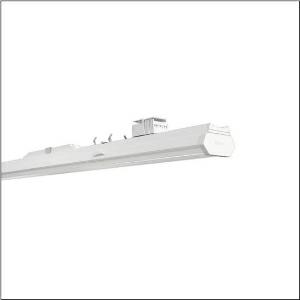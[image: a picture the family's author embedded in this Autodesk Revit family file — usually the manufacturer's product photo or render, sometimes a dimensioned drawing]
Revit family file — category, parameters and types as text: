
# Revit family: licross_21_protected_mo_52tp12dn4a5g3s4
name_source: partatom
category: Lighting Fixtures
units: mm (PartAtom-declared; Revit-internal decimal feet)

## family parameters
Cut with Voids When Loaded = No
Host = Face
Light Source = No
Part Type = Normal
Room Calculation Point = No
Round Connector Dimension = Use Diameter
Shared = No

## types (1)
- --- (1 x LED, 940 lm, 6.8 W, 4000K)
    Apparent Load = 7 VA
    CIE Flux Codes = 73 92 98 99 100
    Color Rendering = 80
    Color Temperature = 4000K
    Default Elevation = 1800 mm
    Description = Licross 21 Protected MO, luminaire insert, of sheet steel, galvanised, coil coated, white, length: 1.500mm, width: 90mm, height: 103mm, LED rated luminous flux: 10.700lm, light colour: 840, SDCM (Standard Deviation of Colour Matching)MacAdam ≤ 3 SDCM (initial), control gear: DALI 2, with plug, 6-pole, with phase selection, for trunking rail, 9 or 11-core, mains connection: 220..240V, AC, 50/60Hz, rated input power: 66W, for trunking rail, 9-/11-core, internal wiring halogen-free, for emergency light function, converter,control gear: single battery element, battery: LiFePO4, 9Ah, primary light control with lens, of plastic, primary optical cover: cover, of PMMA, light emission: direct distribution, primary light characteristic: symmetric, protection rating (complete): IP64, insulation class (complete): insulation class I (protective earthing), certification: CE, UKCA, protection symbol: D if used in an environment with conductive dust loads with corresponding accessories, impact resistance: IK06, permissible ambient temperature for indoor applications: +5..+35°C, standard: EN 60598-2-22, LABS conformity tested according to VDMA 24364:2018-05, reducing of maximum allowable ambient temperature of 5°C with ceiling mounting, corresponds to IFS (International Featured Standards) requirements for safety and quality in the food industry, The light source and the operating device comply with the requirements of the Ecodesign Regulation (EU) 2019/2020 and are replaceable in accordance with this regulation, packaging unit: 1 piece
    Height = 92 mm
    Lamp = 1 x LED
    Lamp Light Flux = 940 lm
    Lamp Power = 6.8 W
    Lamp count = 1
    Length = 1500 mm
    Luminous efficacy = 138 lm/W
    Manufacturer = Siteco
    ModVariant = No
    Model = 52TP12DN4A5G3S4
    Mounting Place = Ceiling
    Mounting Type = Pendant
    Number of Poles = 1
    OnlyDefault = Yes
    Power Factor = 1
    Product Name = Licross 21 Protected MO
    Product group = luminaire insert | ceiling pendant
    ProductGroupID = 901
    Protection Class = Protection class I
    Protection Degree = IP 64
    RLX_Detail_Level = 1
    RLX_Emergency_Light_Flux = 0 lm
    RLX_Emergency_Type = 0
    RLX_Emergency_Type_DB = No
    RlxData = <blob elided: 25177 chars, md5=7f72b670>
    Socket = socket
    Standby Power = 0 W
    System Light Flux = 940 lm
    System Power = 7 W
    Type Comments = : emergency light operation: 3 h
    Type Image = l_1256148.jpg
    URL = http://relux.com
    VarID = @adj_110873
    Voltage = 0 V
    Weight = 0.00 kg
    Width = 88 mm

## geometry (parser evidence)
native form markers: Blend x4, Sweep x9
no freeform markers — native parametric forms only
